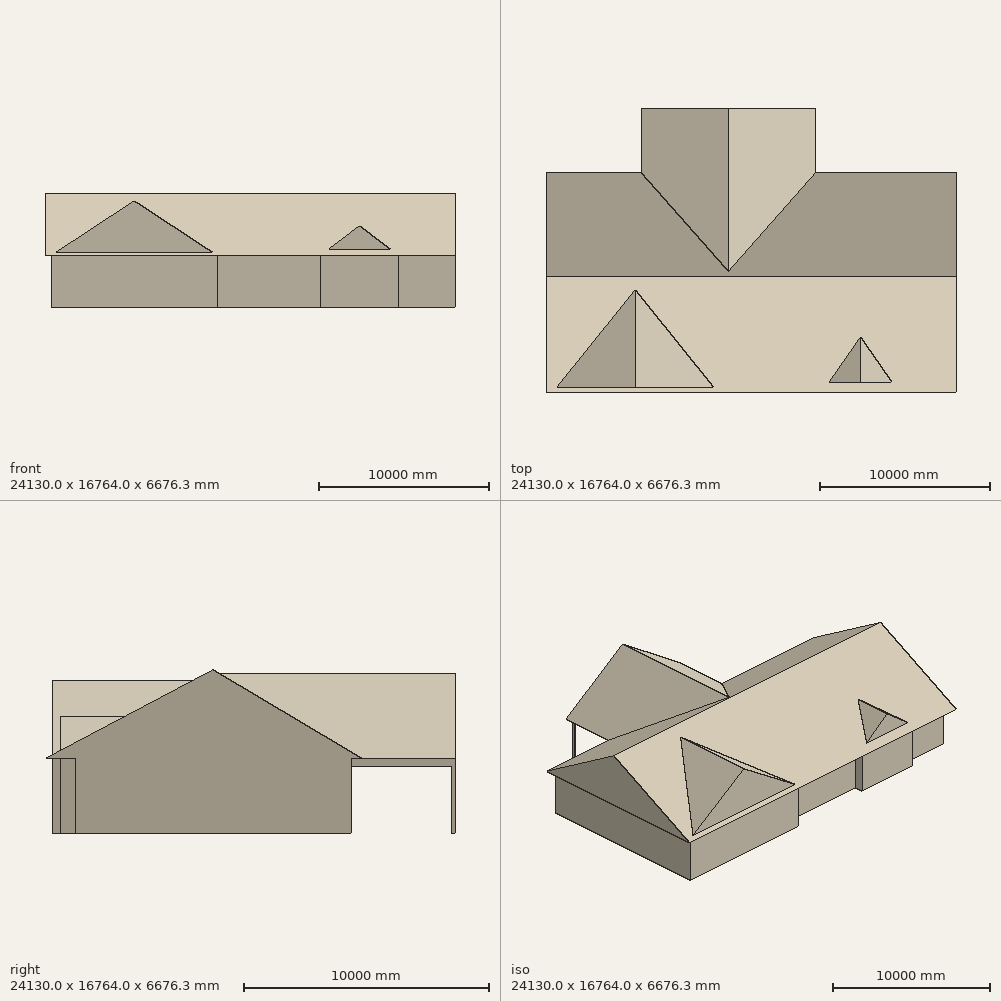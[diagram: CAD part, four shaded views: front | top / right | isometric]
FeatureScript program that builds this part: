
annotation { "Feature Type Name" : "Feature", "Feature Type Description" : "" }
export const myFeature = defineFeature(function(context is Context, id is Id, definition is map)
    precondition{}
    {
        {
            var Q0;
            Q0=qCreatedBy(makeId("Top.planeOp"),FACE);
            var sketch = newSketch(context, id + "F0", { "sketchPlane" : qUnion([Q0])});
            skLineSegment(sketch, "E0.0", {"start": v(-13033.96, -6160.1) * mm, "end": v(-13033.96, 7251.1) * mm});
            skLineSegment(sketch, "E1", {"start": v(-13033.96, 6031.9) * mm, "end": v(-7242.76, 6031.9) * mm});
            skLineSegment(sketch, "E2", {"start": v(-7242.76, 6031.9) * mm, "end": v(-7242.76, 10299.1) * mm});
            skLineSegment(sketch, "E3", {"start": v(-7242.76, 10299.1) * mm, "end": v(1901.24, 10299.1) * mm});
            skLineSegment(sketch, "E4", {"start": v(1901.24, 10299.1) * mm, "end": v(1901.24, 6031.9) * mm});
            skLineSegment(sketch, "E5", {"start": v(1901.24, 6031.9) * mm, "end": v(10740.44, 6031.9) * mm});
            skLineSegment(sketch, "E6", {"start": v(10740.44, 6031.9) * mm, "end": v(10740.44, -5245.7) * mm});
            skLineSegment(sketch, "E7", {"start": v(10740.44, -5245.7) * mm, "end": v(7387.64, -5245.7) * mm});
            skLineSegment(sketch, "E8", {"start": v(7387.64, -5855.3) * mm, "end": v(2815.64, -5855.3) * mm});
            skLineSegment(sketch, "E9", {"start": v(2815.64, -5855.3) * mm, "end": v(2815.64, -5245.7) * mm});
            skLineSegment(sketch, "E10", {"start": v(2815.64, -5245.7) * mm, "end": v(-3280.36, -5245.7) * mm});
            skLineSegment(sketch, "E11", {"start": v(-3280.36, -5245.7) * mm, "end": v(-3280.36, -6160.1) * mm});
            skLineSegment(sketch, "E12.0", {"start": v(-3280.36, -6160.1) * mm, "end": v(-13033.96, -6160.1) * mm});
            skLineSegment(sketch, "E13", {"start": v(7387.64, -5245.7) * mm, "end": v(7387.64, -5855.3) * mm});
            skLineSegment(sketch, "E14", {"start": v(-13033.96, 545.5) * mm, "end": v(10740.44, 545.5) * mm, "construction": true});
            skLineSegment(sketch, "E15", {"start": v(-8157.16, -6160.1) * mm, "end": v(-8157.16, 545.5) * mm, "construction": true});
            skLineSegment(sketch, "E16", {"start": v(-2670.76, 10299.1) * mm, "end": v(-2670.76, 545.5) * mm, "construction": true});
            skLineSegment(sketch, "E17", {"start": v(5101.64, -5855.3) * mm, "end": v(5101.64, 545.5) * mm, "construction": true});
            skSolve(sketch);
        }
        {
            var Q0;
            {var subQ2=sQuery(id+"F0.wireOp",EDGE,"E1");Q0=makeQuery(id+"F0.imprint","IMPRINT",FACE,{"disambiguationData":[TD([[makeQuery(id+"F0.imprint","IMPRINT",EDGE,{"derivedFrom":subQ2}),-1.0]])]});}
            extrude(context, id + "F1", {"entities" : qUnion([Q0]), "depth" : 3048 * mm, "offsetDistance" : 25.4 * mm});
        }
        {
            var Q0;
            Q0=makeQuery(id+"F1.opExtrude","SWEPT_FACE",FACE,{"disambiguationData":[OSD([sQuery(id+"F0.wireOp",EDGE,"E6")])]});
            var sketch = newSketch(context, id + "F2", { "sketchPlane" : qUnion([Q0])});
            skLineSegment(sketch, "E18.0", {"start": v(6031.9, 3048) * mm, "end": v(-5245.7, 3048) * mm});
            skLineSegment(sketch, "E19", {"start": v(393.1, 3048) * mm, "end": v(393.1, 6676.3) * mm});
            skLineSegment(sketch, "E20", {"start": v(393.1, 6676.3) * mm, "end": v(-6464.9, 3048) * mm});
            skLineSegment(sketch, "E21", {"start": v(-6464.9, 3048) * mm, "end": v(393.1, 3048) * mm});
            skLineSegment(sketch, "E22", {"start": v(393.1, 6676.3) * mm, "end": v(6489.1, 3048) * mm});
            skLineSegment(sketch, "E23", {"start": v(6489.1, 3048) * mm, "end": v(393.1, 3048) * mm});
            skSolve(sketch);
        }
        {
            var Q0;
            Q0 = qSketchRegion(id + "F2", true);
            extrude(context, id + "F3", {"entities" : qUnion([Q0]), "operationType" : NewBodyOperationType.ADD, "oppositeDirection" : true, "depth" : 24130 * mm, "offsetDistance" : 25.4 * mm});
        }
        {
            var Q0;
            Q0=makeQuery(id+"F1.opExtrude","SWEPT_FACE",FACE,{"disambiguationData":[OSD([sQuery(id+"F0.wireOp",EDGE,"E12.0")])]});
            var sketch = newSketch(context, id + "F4", { "sketchPlane" : qUnion([Q0])});
            skLineSegment(sketch, "E24", {"start": v(-8157.16, 3048) * mm, "end": v(-8157.16, 6253.3) * mm});
            skLineSegment(sketch, "E25", {"start": v(-8157.16, 6253.3) * mm, "end": v(-13033.96, 3048) * mm});
            skLineSegment(sketch, "E26", {"start": v(-13033.96, 3048) * mm, "end": v(-3280.36, 3048) * mm});
            skLineSegment(sketch, "E27", {"start": v(-3280.36, 3048) * mm, "end": v(-8157.16, 6253.3) * mm});
            skSolve(sketch);
        }
        {
            var Q0;
            {var subQ0=sQuery(id+"F4.wireOp",EDGE,"E24");Q0=makeQuery(id+"F4.imprint","IMPRINT",FACE,{"disambiguationData":[TD([[makeQuery(id+"F4.imprint","IMPRINT",EDGE,{"derivedFrom":subQ0}),1.0]])]});}
            var Q1;
            {var subQ0=sQuery(id+"F4.wireOp",EDGE,"E24");Q1=makeQuery(id+"F4.imprint","IMPRINT",FACE,{"disambiguationData":[TD([[makeQuery(id+"F4.imprint","IMPRINT",EDGE,{"derivedFrom":subQ0}),-1.0]])]});}
            extrude(context, id + "F5", {"entities" : qUnion([Q0, Q1]), "operationType" : NewBodyOperationType.ADD, "oppositeDirection" : true, "depth" : 6553.2 * mm, "offsetDistance" : 25.4 * mm});
        }
        {
            var Q0;
            Q0=makeQuery(id+"F1.opExtrude","SWEPT_FACE",FACE,{"disambiguationData":[OSD([sQuery(id+"F0.wireOp",EDGE,"E8")])]});
            var sketch = newSketch(context, id + "F6", { "sketchPlane" : qUnion([Q0])});
            skLineSegment(sketch, "E28", {"start": v(5101.64, 3048) * mm, "end": v(5101.64, 4786.18) * mm});
            skLineSegment(sketch, "E29", {"start": v(2815.64, 3048) * mm, "end": v(5101.64, 4786.18) * mm});
            skLineSegment(sketch, "E30", {"start": v(7387.64, 3048) * mm, "end": v(5101.64, 4786.18) * mm});
            skLineSegment(sketch, "E31", {"start": v(7387.64, 3048) * mm, "end": v(2815.64, 3048) * mm});
            skSolve(sketch);
        }
        {
            var Q0;
            {var subQ0=sQuery(id+"F6.wireOp",EDGE,"E28");Q0=makeQuery(id+"F6.imprint","IMPRINT",FACE,{"disambiguationData":[TD([[makeQuery(id+"F6.imprint","IMPRINT",EDGE,{"derivedFrom":subQ0}),-1.0]])]});}
            var Q1;
            {var subQ0=sQuery(id+"F6.wireOp",EDGE,"E28");Q1=makeQuery(id+"F6.imprint","IMPRINT",FACE,{"disambiguationData":[TD([[makeQuery(id+"F6.imprint","IMPRINT",EDGE,{"derivedFrom":subQ0}),1.0]])]});}
            extrude(context, id + "F7", {"entities" : qUnion([Q0, Q1]), "operationType" : NewBodyOperationType.ADD, "oppositeDirection" : true, "depth" : 4343.4 * mm, "offsetDistance" : 25.4 * mm});
        }
        {
            var Q0;
            Q0=makeQuery(id+"F1.opExtrude","SWEPT_FACE",FACE,{"disambiguationData":[OSD([sQuery(id+"F0.wireOp",EDGE,"E3")])]});
            var sketch = newSketch(context, id + "F8", { "sketchPlane" : qUnion([Q0])});
            skLineSegment(sketch, "E32", {"start": v(2670.76, 3048) * mm, "end": v(2670.76, 6507.07) * mm});
            skLineSegment(sketch, "E33", {"start": v(2670.76, 6507.07) * mm, "end": v(-2463.05, 3048) * mm});
            skLineSegment(sketch, "E34", {"start": v(-2463.05, 3048) * mm, "end": v(7811.22, 3048) * mm});
            skLineSegment(sketch, "E35", {"start": v(7811.22, 3048) * mm, "end": v(2670.76, 6507.07) * mm});
            skSolve(sketch);
        }
        {
            var Q0;
            {var subQ0=sQuery(id+"F8.wireOp",EDGE,"E32");Q0=makeQuery(id+"F8.imprint","IMPRINT",FACE,{"disambiguationData":[TD([[makeQuery(id+"F8.imprint","IMPRINT",EDGE,{"derivedFrom":subQ0}),1.0]])]});}
            var Q1;
            {var subQ0=sQuery(id+"F8.wireOp",EDGE,"E32");Q1=makeQuery(id+"F8.imprint","IMPRINT",FACE,{"disambiguationData":[TD([[makeQuery(id+"F8.imprint","IMPRINT",EDGE,{"derivedFrom":subQ0}),-1.0]])]});}
            extrude(context, id + "F9", {"entities" : qUnion([Q0, Q1]), "operationType" : NewBodyOperationType.ADD, "oppositeDirection" : true, "depth" : 9779 * mm, "offsetDistance" : 25.4 * mm});
        }
        {
            var Q0;
            Q0=makeQuery(id+"F1.opExtrude","SWEPT_FACE",FACE,{"disambiguationData":[OSD([sQuery(id+"F0.wireOp",EDGE,"E2")])]});
            var sketch = newSketch(context, id + "F10", { "sketchPlane" : qUnion([Q0])});
            skLineSegment(sketch, "E36.0", {"start": v(-6031.9, 2738.12) * mm, "end": v(-10146.7, 2738.12) * mm});
            skLineSegment(sketch, "E37.0", {"start": v(-10146.7, 2738.12) * mm, "end": v(-10146.7, 0) * mm});
            skLineSegment(sketch, "E38", {"start": v(-10146.7, 0) * mm, "end": v(-10087.8, -287) * mm});
            skLineSegment(sketch, "E39", {"start": v(-10087.8, -287) * mm, "end": v(-6031.9, 0) * mm});
            skLineSegment(sketch, "E40", {"start": v(-6031.9, 0) * mm, "end": v(-6031.9, 2738.12) * mm});
            skSolve(sketch);
        }
        {
            var Q0;
            {var subQ0=sQuery(id+"F10.wireOp",EDGE,"E38");Q0=makeQuery(id+"F10.imprint","IMPRINT",FACE,{"disambiguationData":[TD([[makeQuery(id+"F10.imprint","IMPRINT",EDGE,{"derivedFrom":subQ0}),1.0]])]});}
            var Q1;
            Q1=makeQuery(id+"F10.imprint","IMPRINT",FACE,{"disambiguationData":[TD([[makeQuery(id+"F10.imprint","IMPRINT",EDGE,{"derivedFrom":sQuery(id+"F10.wireOp",EDGE,"E36.0")}),1.0]])]});
            extrude(context, id + "F11", {"entities" : qUnion([Q0, Q1]), "operationType" : NewBodyOperationType.REMOVE, "endBound" : BoundingType.THROUGH_ALL, "oppositeDirection" : true, "depth" : 25.4 * mm, "offsetDistance" : 25.4 * mm});
        }
        {
            var Q0;
            Q0=makeQuery(id+"F9.boolean.opBoolean","MERGE",FACE,{"derivedFrom":[makeQuery(id+"F1.opExtrude","SWEPT_FACE",FACE,{"disambiguationData":[OSD([sQuery(id+"F0.wireOp",EDGE,"E3")])]}),makeQuery(id+"F9.opExtrude","CAP_FACE",FACE,{"disambiguationData":[OSD([sQuery(id+"F8.wireOp",EDGE,"E33"),sQuery(id+"F8.wireOp",EDGE,"E34"),sQuery(id+"F8.wireOp",EDGE,"E35")])],"isStart":true})]});
            var sketch = newSketch(context, id + "F12", { "sketchPlane" : qUnion([Q0])});
            skLineSegment(sketch, "E41.0", {"start": v(-1748.84, 3048) * mm, "end": v(-1748.84, 0) * mm});
            skLineSegment(sketch, "E42.0", {"start": v(7090.36, 3048) * mm, "end": v(7090.36, 0) * mm});
            skLineSegment(sketch, "E43", {"start": v(-1748.84, 3048) * mm, "end": v(7090.36, 3048) * mm});
            skLineSegment(sketch, "E44", {"start": v(-1748.84, 0) * mm, "end": v(7090.36, 0) * mm});
            skSolve(sketch);
        }
        {
            var Q0;
            Q0 = qSketchRegion(id + "F12", true);
            extrude(context, id + "F13", {"entities" : qUnion([Q0]), "operationType" : NewBodyOperationType.REMOVE, "oppositeDirection" : true, "depth" : 4267.2 * mm, "offsetDistance" : 25.4 * mm});
        }
    });
